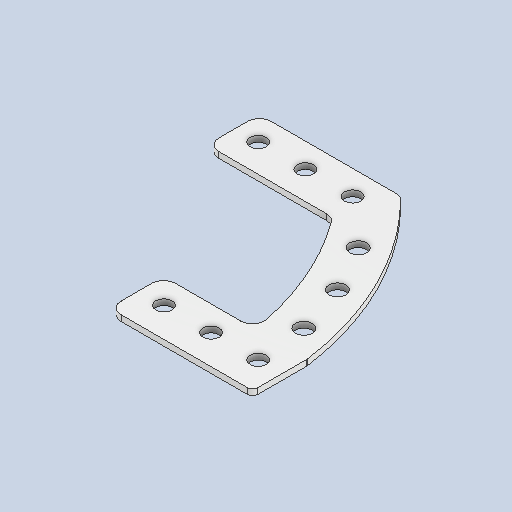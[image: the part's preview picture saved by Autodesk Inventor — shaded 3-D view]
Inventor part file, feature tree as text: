
AUTODESK INVENTOR PART (.ipt)
format: ipt  version: 2025.2 (Build 292293000, 293)  size: 140,800 bytes
history: native  units: in
note: dims shown in document units (in); Inventor stores cm internally (conversion verified against a paired STEP export)
features: other x3, sketch x1
ambient origin geometry x8: Origin, YZ Plane, XZ Plane, XY Plane, X Axis, Y Axis, Z Axis, Center Point
bodies: Solid1 (feature_tree)
feature tree (4):
  other  "Drive_Bumpers.ipt"
  other  "Solid1::Drive_Bumpers.ipt"
  other  "TaggingFeature1"
  sketch  "Sketch1"  dims[d0=0.3937in]
